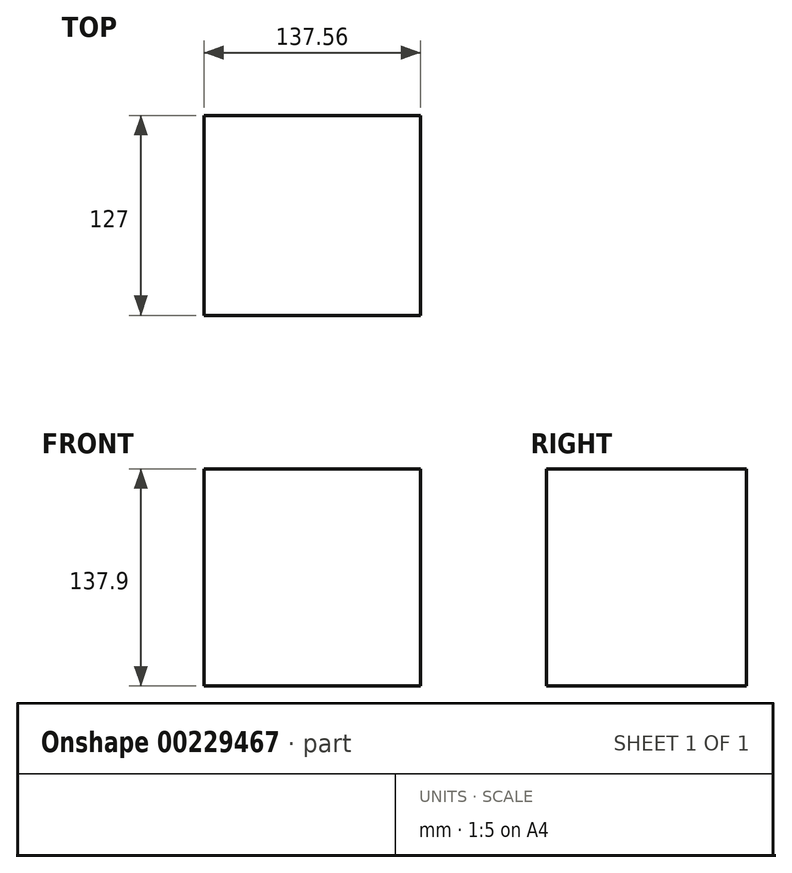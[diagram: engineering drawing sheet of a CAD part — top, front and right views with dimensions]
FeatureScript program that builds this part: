
annotation { "Feature Type Name" : "Feature", "Feature Type Description" : "" }
export const myFeature = defineFeature(function(context is Context, id is Id, definition is map)
    precondition{}
    {
        {
            var Q0;
            Q0=qCreatedBy(makeId("Front.planeOp"),FACE);
            var sketch = newSketch(context, id + "F0", { "sketchPlane" : qUnion([Q0])});
            skLineSegment(sketch, "E0.bottom", {"start": v(68.78, 68.95) * mm, "end": v(-68.78, 68.95) * mm});
            skLineSegment(sketch, "E0.top", {"start": v(68.78, -68.95) * mm, "end": v(-68.78, -68.95) * mm});
            skLineSegment(sketch, "E0.left", {"start": v(68.78, 68.95) * mm, "end": v(68.78, -68.95) * mm});
            skLineSegment(sketch, "E0.right", {"start": v(-68.78, 68.95) * mm, "end": v(-68.78, -68.95) * mm});
            skPoint(sketch, "E0.middle", {"position": v(0, 0) * mm});
            skSolve(sketch);
        }
        {
            var Q0;
            Q0=makeQuery(id+"F0.imprint","IMPRINT",FACE,{"disambiguationData":[TD([[makeQuery(id+"F0.imprint","IMPRINT",EDGE,{"derivedFrom":sQuery(id+"F0.wireOp",EDGE,"E0.bottom")}),1.0]])]});
            extrude(context, id + "F1", {"entities" : qUnion([Q0]), "endBound" : BoundingType.SYMMETRIC, "depth" : 127 * mm});
        }
    });
